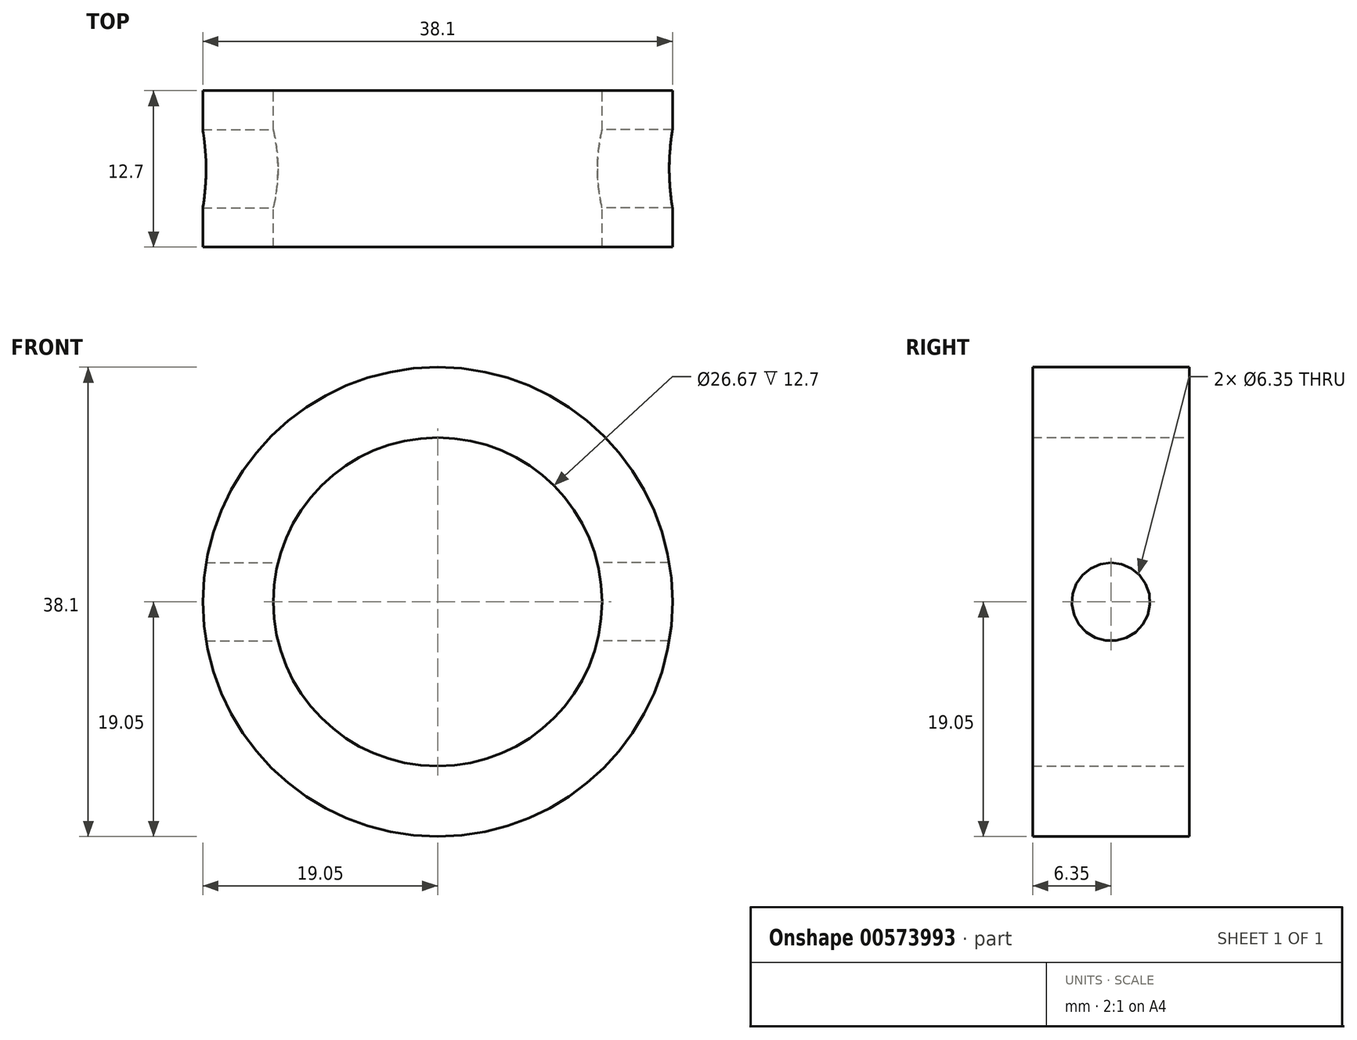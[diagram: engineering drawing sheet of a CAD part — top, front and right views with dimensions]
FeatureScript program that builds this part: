
annotation { "Feature Type Name" : "Feature", "Feature Type Description" : "" }
export const myFeature = defineFeature(function(context is Context, id is Id, definition is map)
    precondition{}
    {
        {
            var Q0;
            Q0=qCreatedBy(makeId("Front.planeOp"),FACE);
            var sketch = newSketch(context, id + "F0", { "sketchPlane" : qUnion([Q0])});
            skCircle(sketch, "E0", {"center": v(0, 0) * mm, "radius": 13.34 * mm});
            skCircle(sketch, "E1", {"center": v(0, 0) * mm, "radius": 19.05 * mm});
            skSolve(sketch);
        }
        {
            var Q0;
            Q0=makeQuery(id+"F0.imprint","IMPRINT",FACE,{"disambiguationData":[TD([[makeQuery(id+"F0.imprint","IMPRINT",EDGE,{"derivedFrom":sQuery(id+"F0.wireOp",EDGE,"E0")}),-1.0]])]});
            extrude(context, id + "F1", {"entities" : qUnion([Q0]), "endBound" : BoundingType.SYMMETRIC, "depth" : 12.7 * mm, "offsetDistance" : 25.4 * mm});
        }
        {
            var Q0;
            Q0=qCreatedBy(makeId("Right.planeOp"),FACE);
            var sketch = newSketch(context, id + "F2", { "sketchPlane" : qUnion([Q0])});
            skCircle(sketch, "E2", {"center": v(0, 0) * mm, "radius": 3.18 * mm});
            skSolve(sketch);
        }
        {
            var Q0;
            Q0=sQuery(id+"F2.wireOp",VERTEX,"E2.center");
            var Q1;
            Q1=makeQuery(id+"F1.opExtrude","SWEPT_BODY",BODY,{"disambiguationData":[OSD([sQuery(id+"F0.wireOp",EDGE,"E0"),sQuery(id+"F0.wireOp",EDGE,"E1")])]});
            hole(context, id + "F3", {"style" : HoleStyle.SIMPLE, "endStyle" : HoleEndStyle.THROUGH, "oppositeDirection" : true, "holeDiameter" : 6.35 * mm, "isTappedThrough" : true, "tappedDepth" : 12.7 * mm, "tapClearance" : 3, "locations" : qUnion([Q0]), "scope" : qUnion([Q1])});
        }
        {
            var Q0;
            Q0=sQuery(id+"F2.wireOp",VERTEX,"E2.center");
            var Q1;
            Q1=makeQuery(id+"F1.opExtrude","SWEPT_BODY",BODY,{"disambiguationData":[OSD([sQuery(id+"F0.wireOp",EDGE,"E0"),sQuery(id+"F0.wireOp",EDGE,"E1")])]});
            hole(context, id + "F4", {"style" : HoleStyle.SIMPLE, "endStyle" : HoleEndStyle.THROUGH, "holeDiameter" : 6.35 * mm, "isTappedThrough" : true, "tappedDepth" : 12.7 * mm, "tapClearance" : 3, "locations" : qUnion([Q0]), "scope" : qUnion([Q1])});
        }
    });
